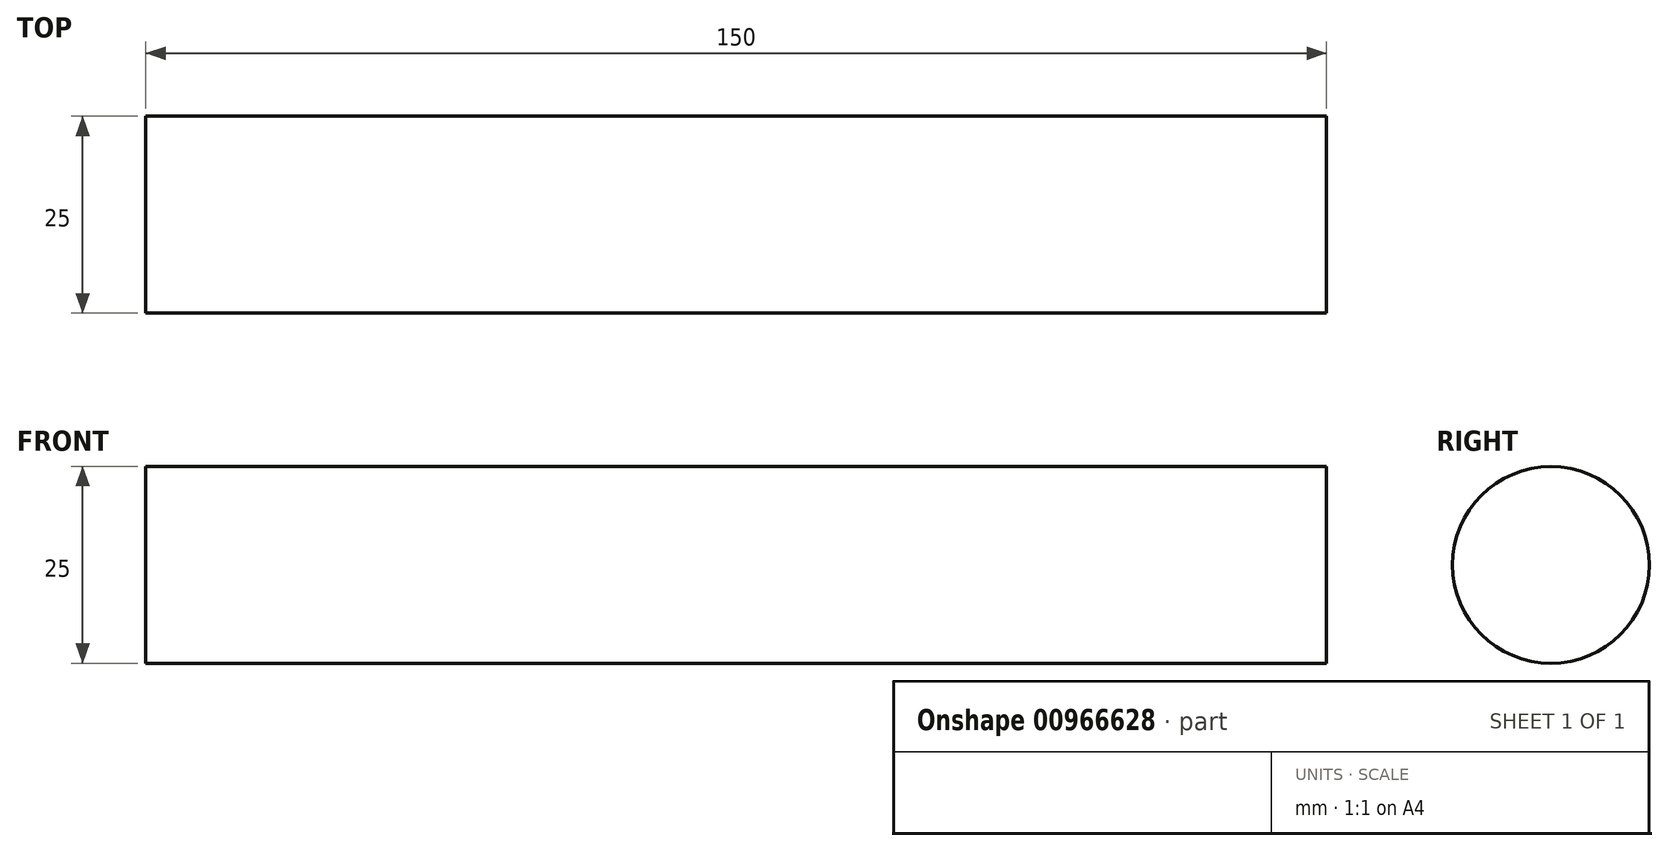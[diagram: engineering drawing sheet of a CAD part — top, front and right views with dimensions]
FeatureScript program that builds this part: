
annotation { "Feature Type Name" : "Feature", "Feature Type Description" : "" }
export const myFeature = defineFeature(function(context is Context, id is Id, definition is map)
    precondition{}
    {
        {
            var Q0;
            Q0=qCreatedBy(makeId("Right.planeOp"),FACE);
            var sketch = newSketch(context, id + "F0", { "sketchPlane" : qUnion([Q0])});
            skCircle(sketch, "E0", {"center": v(0, 0) * mm, "radius": 12.5 * mm});
            skSolve(sketch);
        }
        {
            var Q0;
            Q0 = qSketchRegion(id + "F0", true);
            extrude(context, id + "F1", {"entities" : qUnion([Q0]), "oppositeDirection" : true, "depth" : 150 * mm, "offsetDistance" : 25 * mm});
        }
    });
